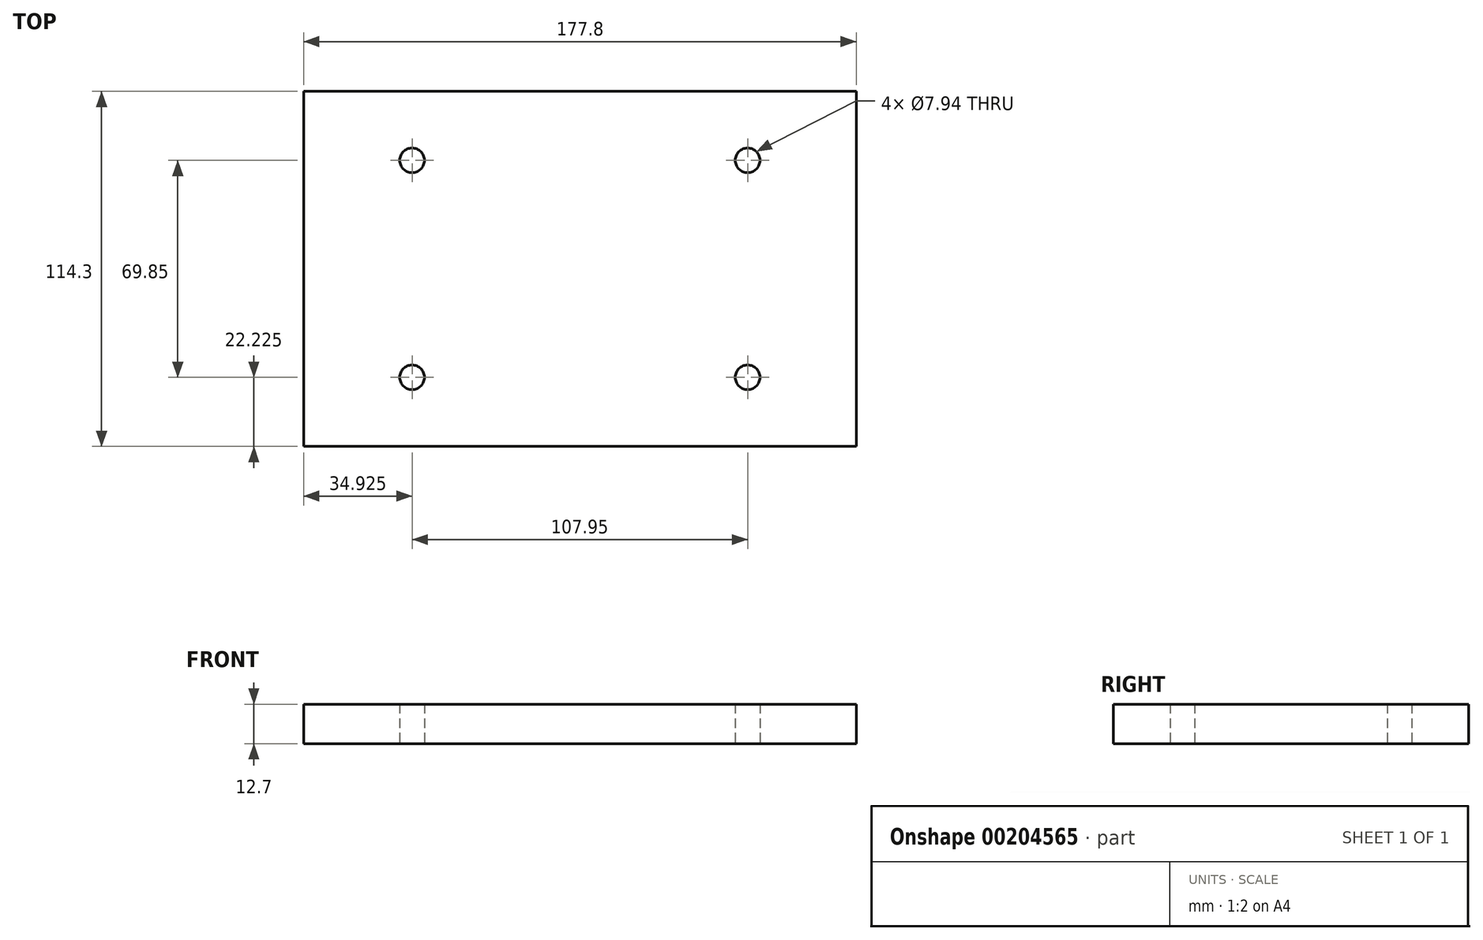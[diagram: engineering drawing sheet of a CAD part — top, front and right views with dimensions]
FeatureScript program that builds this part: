
annotation { "Feature Type Name" : "Feature", "Feature Type Description" : "" }
export const myFeature = defineFeature(function(context is Context, id is Id, definition is map)
    precondition{}
    {
        {
            var Q0;
            Q0=qCreatedBy(makeId("Top.planeOp"),FACE);
            var sketch = newSketch(context, id + "F0", { "sketchPlane" : qUnion([Q0])});
            skLineSegment(sketch, "E0.bottom", {"start": v(-88.9, 57.15) * mm, "end": v(88.9, 57.15) * mm});
            skLineSegment(sketch, "E0.top", {"start": v(-88.9, -57.15) * mm, "end": v(88.9, -57.15) * mm});
            skLineSegment(sketch, "E0.left", {"start": v(-88.9, 57.15) * mm, "end": v(-88.9, -57.15) * mm});
            skLineSegment(sketch, "E0.right", {"start": v(88.9, 57.15) * mm, "end": v(88.9, -57.15) * mm});
            skPoint(sketch, "E0.middle", {"position": v(0, 0) * mm});
            skLineSegment(sketch, "E1.bottom", {"start": v(-53.97, 34.93) * mm, "end": v(53.98, 34.93) * mm, "construction": true});
            skLineSegment(sketch, "E1.top", {"start": v(-53.98, -34.93) * mm, "end": v(53.97, -34.93) * mm, "construction": true});
            skLineSegment(sketch, "E1.left", {"start": v(-53.97, 34.93) * mm, "end": v(-53.98, -34.93) * mm, "construction": true});
            skLineSegment(sketch, "E1.right", {"start": v(53.98, 34.93) * mm, "end": v(53.97, -34.93) * mm, "construction": true});
            skCircle(sketch, "E2", {"center": v(-53.97, 34.93) * mm, "radius": 3.97 * mm});
            skCircle(sketch, "E3", {"center": v(53.98, 34.93) * mm, "radius": 3.97 * mm});
            skCircle(sketch, "E4", {"center": v(53.97, -34.93) * mm, "radius": 3.97 * mm});
            skCircle(sketch, "E5", {"center": v(-53.98, -34.93) * mm, "radius": 3.97 * mm});
            skSolve(sketch);
        }
        {
            var Q0;
            Q0 = qSketchRegion(id + "F0", true);
            extrude(context, id + "F1", {"entities" : qUnion([Q0]), "depth" : 12.7 * mm});
        }
    });
